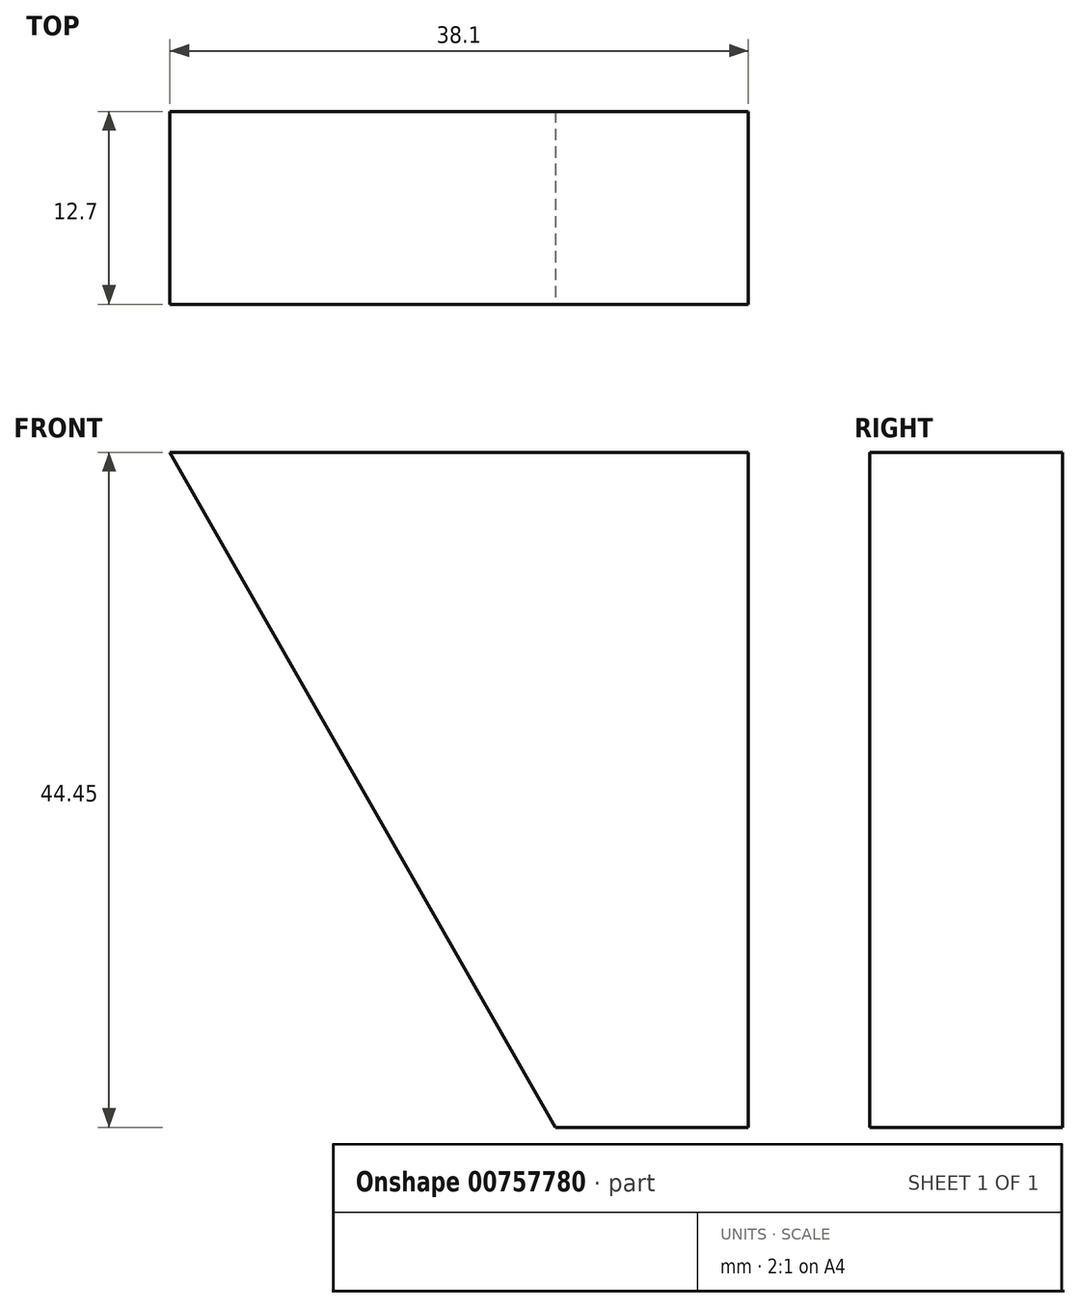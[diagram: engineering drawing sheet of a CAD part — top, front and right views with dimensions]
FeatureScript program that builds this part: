
annotation { "Feature Type Name" : "Feature", "Feature Type Description" : "" }
export const myFeature = defineFeature(function(context is Context, id is Id, definition is map)
    precondition{}
    {
        {
            var Q0;
            Q0=qCreatedBy(makeId("Front.planeOp"),FACE);
            var sketch = newSketch(context, id + "F0", { "sketchPlane" : qUnion([Q0])});
            skLineSegment(sketch, "E0", {"start": v(-29.61, 0) * mm, "end": v(27.54, 0) * mm});
            skLineSegment(sketch, "E1", {"start": v(27.54, 0) * mm, "end": v(27.54, 44.45) * mm});
            skLineSegment(sketch, "E2", {"start": v(27.54, 44.45) * mm, "end": v(-29.61, 44.45) * mm});
            skLineSegment(sketch, "E3", {"start": v(-29.61, 44.45) * mm, "end": v(-29.61, 0) * mm});
            skSolve(sketch);
        }
        {
            var Q0;
            Q0 = qSketchRegion(id + "F0", true);
            extrude(context, id + "F1", {"entities" : qUnion([Q0]), "depth" : 25.4 * mm, "offsetDistance" : 25.4 * mm});
        }
        {
            var Q0;
            Q0=makeQuery(id+"F1.opExtrude","CAP_FACE",FACE,{"disambiguationData":[OSD([sQuery(id+"F0.wireOp",EDGE,"E0"),sQuery(id+"F0.wireOp",EDGE,"E1"),sQuery(id+"F0.wireOp",EDGE,"E2"),sQuery(id+"F0.wireOp",EDGE,"E3")])],"isStart":false});
            var sketch = newSketch(context, id + "F2", { "sketchPlane" : qUnion([Q0])});
            skLineSegment(sketch, "E4", {"start": v(-4.21, 44.45) * mm, "end": v(-4.21, 0) * mm});
            skCircle(sketch, "E5", {"center": v(-4.21, 22.23) * mm, "radius": 12.7 * mm});
            skLineSegment(sketch, "E6", {"start": v(14.84, 0) * mm, "end": v(-10.56, 44.45) * mm});
            skSolve(sketch);
        }
        {
            var Q0;
            {var subQ0=sQuery(id+"F2.wireOp",EDGE,"E5");var subQ1=sQuery(id+"F2.wireOp",EDGE,"E4");var subQ2=makeQuery(id+"F2.imprint","INTERSECT",VERTEX,{"disambiguationData":[OD(0.0)],"derivedFrom":[subQ1,subQ0]});Q0=makeQuery(id+"F2.imprint","IMPRINT",FACE,{"disambiguationData":[TD([[makeQuery(id+"F2.imprint","IMPRINT",EDGE,{"disambiguationData":[TD([[subQ2,-1.0]])],"derivedFrom":subQ1}),-1.0]])]});}
            var Q1;
            {var subQ0=sQuery(id+"F2.wireOp",EDGE,"E6");var subQ1=sQuery(id+"F2.wireOp",EDGE,"E4");var subQ2=makeQuery(id+"F2.imprint","INTERSECT",VERTEX,{"derivedFrom":[subQ1,subQ0]});Q1=makeQuery(id+"F2.imprint","IMPRINT",FACE,{"disambiguationData":[TD([[makeQuery(id+"F2.imprint","IMPRINT",EDGE,{"disambiguationData":[TD([[subQ2,-1.0]])],"derivedFrom":subQ1}),1.0]])]});}
            var Q2;
            {var subQ0=sQuery(id+"F2.wireOp",EDGE,"E5");var subQ1=sQuery(id+"F2.wireOp",EDGE,"E4");var subQ2=makeQuery(id+"F2.imprint","INTERSECT",VERTEX,{"disambiguationData":[OD(0.0)],"derivedFrom":[subQ1,subQ0]});Q2=makeQuery(id+"F2.imprint","IMPRINT",FACE,{"disambiguationData":[TD([[makeQuery(id+"F2.imprint","IMPRINT",EDGE,{"disambiguationData":[TD([[subQ2,-1.0]])],"derivedFrom":subQ1}),1.0]])]});}
            var Q3;
            {var subQ0=sQuery(id+"F2.wireOp",EDGE,"E6");var subQ1=sQuery(id+"F2.wireOp",EDGE,"E4");var subQ2=makeQuery(id+"F2.imprint","INTERSECT",VERTEX,{"derivedFrom":[subQ1,subQ0]});Q3=makeQuery(id+"F2.imprint","IMPRINT",FACE,{"disambiguationData":[TD([[makeQuery(id+"F2.imprint","IMPRINT",EDGE,{"disambiguationData":[TD([[subQ2,-1.0]])],"derivedFrom":subQ1}),-1.0]])]});}
            extrude(context, id + "F3", {"entities" : qUnion([Q0, Q1, Q2, Q3]), "operationType" : NewBodyOperationType.REMOVE, "endBound" : BoundingType.THROUGH_ALL, "oppositeDirection" : true, "depth" : 12.7 * mm, "offsetDistance" : 25.4 * mm});
        }
        {
            var Q0;
            Q0=makeQuery(id+"F1.opExtrude","CAP_FACE",FACE,{"disambiguationData":[OSD([sQuery(id+"F0.wireOp",EDGE,"E0"),sQuery(id+"F0.wireOp",EDGE,"E1"),sQuery(id+"F0.wireOp",EDGE,"E2"),sQuery(id+"F0.wireOp",EDGE,"E3")])],"isStart":false});
            var sketch = newSketch(context, id + "F4", { "sketchPlane" : qUnion([Q0])});
            skLineSegment(sketch, "E7", {"start": v(14.84, 0) * mm, "end": v(-10.56, 44.45) * mm});
            skSolve(sketch);
        }
        {
            var Q0;
            Q0 = qSketchRegion(id + "F4", true);
            var Q1;
            {var subQ0=makeQuery(id+"F1.opExtrude","CAP_EDGE",EDGE,{"disambiguationData":[OSD([sQuery(id+"F0.wireOp",EDGE,"E1")])],"isStart":false});Q1=makeQuery(id+"F4.imprint","IMPRINT",FACE,{"disambiguationData":[TD([[makeQuery(id+"F4.imprint","IMPRINT",EDGE,{"derivedFrom":subQ0}),1.0]])]});}
            extrude(context, id + "F5", {"entities" : qUnion([Q0, Q1]), "operationType" : NewBodyOperationType.REMOVE, "oppositeDirection" : true, "depth" : 12.7 * mm, "offsetDistance" : 25.4 * mm});
        }
    });
